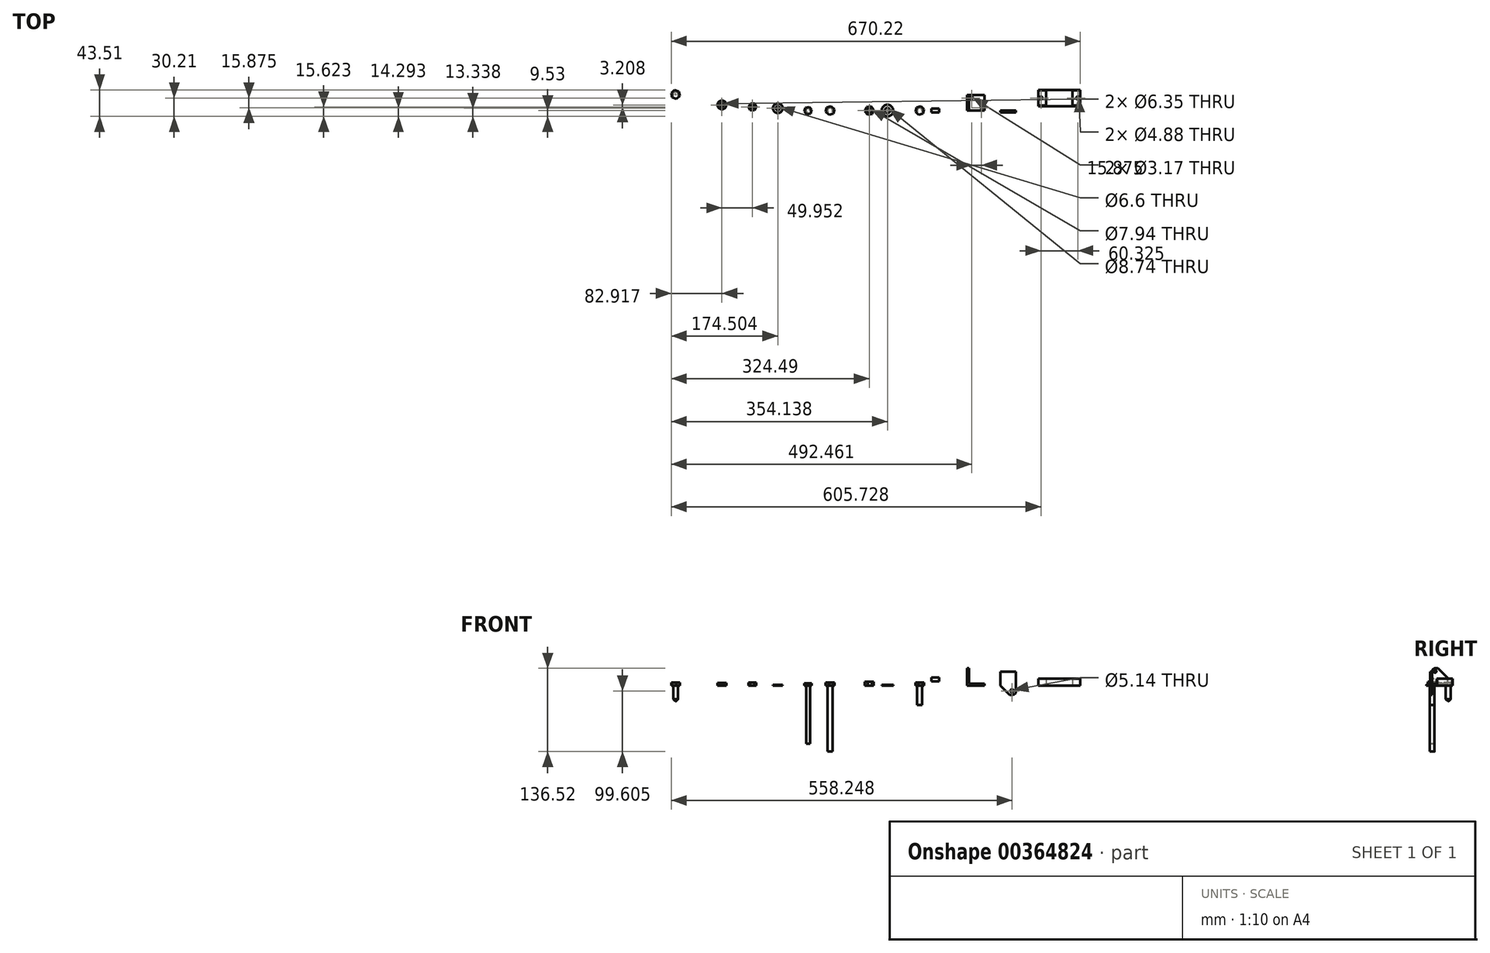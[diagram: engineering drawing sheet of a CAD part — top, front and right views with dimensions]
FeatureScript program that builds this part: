
annotation { "Feature Type Name" : "Feature", "Feature Type Description" : "" }
export const myFeature = defineFeature(function(context is Context, id is Id, definition is map)
    precondition{}
    {
        {
            var Q0;
            Q0=qCreatedBy(makeId("Right.planeOp"),FACE);
            var sketch = newSketch(context, id + "F0", { "sketchPlane" : qUnion([Q0])});
            skCircle(sketch, "E0", {"center": v(0, 10.34) * mm, "radius": 3.18 * mm});
            skSolve(sketch);
        }
        {
            var Q0;
            Q0 = qSketchRegion(id + "F0", true);
            extrude(context, id + "F1", {"entities" : qUnion([Q0]), "depth" : 12.7 * mm, "offsetDistance" : 25.4 * mm});
        }
        {
            var Q0;
            Q0=qCreatedBy(makeId("Top.planeOp"),FACE);
            var sketch = newSketch(context, id + "F2", { "sketchPlane" : qUnion([Q0])});
            skCircle(sketch, "E1", {"center": v(-19.1, 0) * mm, "radius": 3.97 * mm});
            skSolve(sketch);
        }
        {
            var Q0;
            Q0 = qSketchRegion(id + "F2", true);
            extrude(context, id + "F3", {"entities" : qUnion([Q0]), "oppositeDirection" : true, "depth" : 31.75 * mm, "offsetDistance" : 25.4 * mm});
        }
        {
            var Q0;
            Q0=makeQuery(id+"F3.opExtrude","CAP_FACE",FACE,{"disambiguationData":[OSD([sQuery(id+"F2.wireOp",EDGE,"E1")])],"isStart":true});
            var sketch = newSketch(context, id + "F4", { "sketchPlane" : qUnion([Q0])});
            skCircle(sketch, "E2.cCircle", {"center": v(-19.1, 0) * mm, "radius": 6.35 * mm, "construction": true});
            skLineSegment(sketch, "E2.0", {"start": v(-17.16, 7.07) * mm, "end": v(-12, 1.85) * mm});
            skLineSegment(sketch, "E2.1", {"start": v(-12, 1.85) * mm, "end": v(-13.95, -5.22) * mm});
            skLineSegment(sketch, "E2.2", {"start": v(-13.95, -5.22) * mm, "end": v(-21.04, -7.07) * mm});
            skLineSegment(sketch, "E2.3", {"start": v(-21.04, -7.07) * mm, "end": v(-26.2, -1.85) * mm});
            skLineSegment(sketch, "E2.4", {"start": v(-26.2, -1.85) * mm, "end": v(-24.25, 5.22) * mm});
            skLineSegment(sketch, "E2.5", {"start": v(-24.25, 5.22) * mm, "end": v(-17.16, 7.07) * mm});
            skPoint(sketch, "E2.0.midPoint", {"position": v(-14.58, 4.46) * mm});
            skSolve(sketch);
        }
        {
            var Q0;
            Q0=makeQuery(id+"F4.imprint","IMPRINT",FACE,{"disambiguationData":[TD([[makeQuery(id+"F4.imprint","IMPRINT",EDGE,{"derivedFrom":makeQuery(id+"F3.opExtrude","CAP_EDGE",EDGE,{"disambiguationData":[OSD([sQuery(id+"F2.wireOp",EDGE,"E1")])],"isStart":true})}),1.0]])]});
            var Q1;
            Q1=makeQuery(id+"F4.imprint","IMPRINT",FACE,{"disambiguationData":[TD([[makeQuery(id+"F4.imprint","IMPRINT",EDGE,{"derivedFrom":sQuery(id+"F4.wireOp",EDGE,"E2.0")}),-1.0]])]});
            extrude(context, id + "F5", {"entities" : qUnion([Q0, Q1]), "operationType" : NewBodyOperationType.ADD, "depth" : 5.16 * mm, "offsetDistance" : 25.4 * mm});
        }
        {
            var Q0;
            Q0=qCreatedBy(makeId("Top.planeOp"),FACE);
            var sketch = newSketch(context, id + "F6", { "sketchPlane" : qUnion([Q0])});
            skCircle(sketch, "E3", {"center": v(-71.95, 0) * mm, "radius": 9.53 * mm});
            skCircle(sketch, "E4", {"center": v(-71.95, 0) * mm, "radius": 4.37 * mm});
            skSolve(sketch);
        }
        {
            var Q0;
            Q0 = qSketchRegion(id + "F6", true);
            extrude(context, id + "F7", {"entities" : qUnion([Q0]), "depth" : 1.27 * mm, "offsetDistance" : 25.4 * mm});
        }
        {
            var Q0;
            Q0=qCreatedBy(makeId("Top.planeOp"),FACE);
            var sketch = newSketch(context, id + "F8", { "sketchPlane" : qUnion([Q0])});
            skCircle(sketch, "E5.cCircle", {"center": v(-101.6, 0) * mm, "radius": 6.35 * mm, "construction": true});
            skLineSegment(sketch, "E5.0", {"start": v(-98.93, 6.83) * mm, "end": v(-94.35, 1.1) * mm});
            skLineSegment(sketch, "E5.1", {"start": v(-94.35, 1.1) * mm, "end": v(-97.02, -5.73) * mm});
            skLineSegment(sketch, "E5.2", {"start": v(-97.02, -5.73) * mm, "end": v(-104.27, -6.83) * mm});
            skLineSegment(sketch, "E5.3", {"start": v(-104.27, -6.83) * mm, "end": v(-108.85, -1.1) * mm});
            skLineSegment(sketch, "E5.4", {"start": v(-108.85, -1.1) * mm, "end": v(-106.18, 5.73) * mm});
            skLineSegment(sketch, "E5.5", {"start": v(-106.18, 5.73) * mm, "end": v(-98.93, 6.83) * mm});
            skPoint(sketch, "E5.0.midPoint", {"position": v(-96.64, 3.97) * mm});
            skCircle(sketch, "E6", {"center": v(-101.6, 0) * mm, "radius": 3.97 * mm});
            skSolve(sketch);
        }
        {
            var Q0;
            Q0 = qSketchRegion(id + "F8", true);
            extrude(context, id + "F9", {"entities" : qUnion([Q0]), "depth" : 6.75 * mm, "offsetDistance" : 25.4 * mm});
        }
        {
            var Q0;
            Q0=qCreatedBy(makeId("Front.planeOp"),FACE);
            var sketch = newSketch(context, id + "F10", { "sketchPlane" : qUnion([Q0])});
            skLineSegment(sketch, "E7", {"start": v(58.43, 28.58) * mm, "end": v(58.43, 0) * mm});
            skLineSegment(sketch, "E8", {"start": v(58.43, 0) * mm, "end": v(87, 0) * mm});
            skLineSegment(sketch, "E9", {"start": v(87, 0) * mm, "end": v(87, 3.18) * mm});
            skLineSegment(sketch, "E10", {"start": v(87, 3.18) * mm, "end": v(61.6, 3.17) * mm});
            skLineSegment(sketch, "E11", {"start": v(61.6, 3.17) * mm, "end": v(61.6, 28.58) * mm});
            skLineSegment(sketch, "E12", {"start": v(61.6, 28.58) * mm, "end": v(58.43, 28.58) * mm});
            skSolve(sketch);
        }
        {
            var Q0;
            Q0 = qSketchRegion(id + "F10", true);
            extrude(context, id + "F11", {"entities" : qUnion([Q0]), "oppositeDirection" : true, "depth" : 25.4 * mm, "offsetDistance" : 25.4 * mm});
        }
        {
            var Q0;
            Q0=makeQuery(id+"F11.opExtrude","SWEPT_FACE",FACE,{"disambiguationData":[OSD([sQuery(id+"F10.wireOp",EDGE,"E10")])]});
            var sketch = newSketch(context, id + "F12", { "sketchPlane" : qUnion([Q0])});
            skLineSegment(sketch, "E13.bottom", {"start": v(66.37, 20.64) * mm, "end": v(82.25, 20.64) * mm, "construction": true});
            skLineSegment(sketch, "E13.top", {"start": v(66.37, 4.76) * mm, "end": v(82.25, 4.76) * mm, "construction": true});
            skLineSegment(sketch, "E13.left", {"start": v(66.37, 20.64) * mm, "end": v(66.37, 4.76) * mm, "construction": true});
            skLineSegment(sketch, "E13.right", {"start": v(82.25, 20.64) * mm, "end": v(82.25, 4.76) * mm, "construction": true});
            skCircle(sketch, "E14", {"center": v(66.37, 20.64) * mm, "radius": 1.59 * mm});
            skCircle(sketch, "E15", {"center": v(82.25, 4.76) * mm, "radius": 1.59 * mm});
            skSolve(sketch);
        }
        {
            var Q0;
            Q0 = qSketchRegion(id + "F12", true);
            extrude(context, id + "F13", {"entities" : qUnion([Q0]), "operationType" : NewBodyOperationType.REMOVE, "oppositeDirection" : true, "depth" : 25.4 * mm, "offsetDistance" : 25.4 * mm});
        }
        {
            var Q0;
            Q0=makeQuery(id+"F11.opExtrude","SWEPT_FACE",FACE,{"disambiguationData":[OSD([sQuery(id+"F10.wireOp",EDGE,"E7")])]});
            var sketch = newSketch(context, id + "F14", { "sketchPlane" : qUnion([Q0])});
            skCircle(sketch, "E16", {"center": v(-4.76, 23.81) * mm, "radius": 2.38 * mm});
            skSolve(sketch);
        }
        {
            var Q0;
            Q0 = qSketchRegion(id + "F14", true);
            extrude(context, id + "F15", {"entities" : qUnion([Q0]), "operationType" : NewBodyOperationType.REMOVE, "oppositeDirection" : true, "depth" : 25.4 * mm, "offsetDistance" : 25.4 * mm});
        }
        {
            var Q0;
            Q0=makeQuery(id+"F11.opExtrude","CAP_EDGE",EDGE,{"disambiguationData":[OSD([sQuery(id+"F10.wireOp",EDGE,"E12")])],"isStart":true});
            fillet(context, id + "F16", {"entities" : qUnion([Q0]), "radius" : 5.08 * mm, "tangentPropagation" : true, "allowEdgeOverflow" : false});
        }
        {
            var Q0;
            Q0=makeQuery(id+"F11.opExtrude","CAP_EDGE",EDGE,{"disambiguationData":[OSD([sQuery(id+"F10.wireOp",EDGE,"E12")])],"isStart":false});
            chamfer(context, id + "F17", {"entities" : qUnion([Q0]), "width" : 15.88 * mm, "tangentPropagation" : true});
        }
        {
            var Q0;
            Q0=qCreatedBy(makeId("Front.planeOp"),FACE);
            var sketch = newSketch(context, id + "F18", { "sketchPlane" : qUnion([Q0])});
            skLineSegment(sketch, "E17.bottom", {"start": v(113.1, 23.4) * mm, "end": v(138.5, 23.4) * mm});
            skLineSegment(sketch, "E17.top", {"start": v(113.1, -14.7) * mm, "end": v(138.5, -14.7) * mm});
            skLineSegment(sketch, "E17.left", {"start": v(113.1, 23.4) * mm, "end": v(113.1, -14.7) * mm});
            skLineSegment(sketch, "E17.right", {"start": v(138.5, 23.4) * mm, "end": v(138.5, -14.7) * mm});
            skSolve(sketch);
        }
        {
            var Q0;
            Q0 = qSketchRegion(id + "F18", true);
            extrude(context, id + "F19", {"entities" : qUnion([Q0]), "depth" : 3.17 * mm, "offsetDistance" : 25.4 * mm});
        }
        {
            var Q0;
            Q0=makeQuery(id+"F19.opExtrude","CAP_FACE",FACE,{"disambiguationData":[OSD([sQuery(id+"F18.wireOp",EDGE,"E17.bottom"),sQuery(id+"F18.wireOp",EDGE,"E17.top"),sQuery(id+"F18.wireOp",EDGE,"E17.left"),sQuery(id+"F18.wireOp",EDGE,"E17.right")])],"isStart":false});
            var sketch = newSketch(context, id + "F20", { "sketchPlane" : qUnion([Q0])});
            skCircle(sketch, "E18", {"center": v(132.16, -8.34) * mm, "radius": 2.57 * mm});
            skSolve(sketch);
        }
        {
            var Q0;
            Q0 = qSketchRegion(id + "F20", true);
            extrude(context, id + "F21", {"entities" : qUnion([Q0]), "operationType" : NewBodyOperationType.REMOVE, "oppositeDirection" : true, "depth" : 25.4 * mm, "offsetDistance" : 25.4 * mm});
        }
        {
            var Q0;
            Q0=makeQuery(id+"F19.opExtrude","SWEPT_EDGE",EDGE,{"disambiguationData":[OSD([sQuery(id+"F18.wireOp",EDGE,"E17.top"),sQuery(id+"F18.wireOp",EDGE,"E17.right")])]});
            fillet(context, id + "F22", {"entities" : qUnion([Q0]), "radius" : 5.08 * mm, "tangentPropagation" : true, "allowEdgeOverflow" : false});
        }
        {
            var Q0;
            Q0=makeQuery(id+"F19.opExtrude","SWEPT_EDGE",EDGE,{"disambiguationData":[OSD([sQuery(id+"F18.wireOp",EDGE,"E17.top"),sQuery(id+"F18.wireOp",EDGE,"E17.left")])]});
            chamfer(context, id + "F23", {"entities" : qUnion([Q0]), "width" : 15.24 * mm, "tangentPropagation" : true});
        }
        {
            var Q0;
            Q0=qCreatedBy(makeId("Top.planeOp"),FACE);
            var sketch = newSketch(context, id + "F24", { "sketchPlane" : qUnion([Q0])});
            skCircle(sketch, "E19", {"center": v(-165.9, 0) * mm, "radius": 3.97 * mm});
            skSolve(sketch);
        }
        {
            var Q0;
            Q0 = qSketchRegion(id + "F24", true);
            extrude(context, id + "F25", {"entities" : qUnion([Q0]), "oppositeDirection" : true, "depth" : 107.95 * mm, "offsetDistance" : 25.4 * mm});
        }
        {
            var Q0;
            Q0=makeQuery(id+"F25.opExtrude","CAP_FACE",FACE,{"disambiguationData":[OSD([sQuery(id+"F24.wireOp",EDGE,"E19")])],"isStart":true});
            var sketch = newSketch(context, id + "F26", { "sketchPlane" : qUnion([Q0])});
            skCircle(sketch, "E20.cCircle", {"center": v(-165.9, 0) * mm, "radius": 6.35 * mm, "construction": true});
            skLineSegment(sketch, "E20.0", {"start": v(-164.1, 7.1) * mm, "end": v(-158.84, 2) * mm});
            skLineSegment(sketch, "E20.1", {"start": v(-158.84, 2) * mm, "end": v(-160.64, -5.12) * mm});
            skLineSegment(sketch, "E20.2", {"start": v(-160.64, -5.12) * mm, "end": v(-167.7, -7.1) * mm});
            skLineSegment(sketch, "E20.3", {"start": v(-167.7, -7.1) * mm, "end": v(-172.95, -2) * mm});
            skLineSegment(sketch, "E20.4", {"start": v(-172.95, -2) * mm, "end": v(-171.15, 5.12) * mm});
            skLineSegment(sketch, "E20.5", {"start": v(-171.15, 5.12) * mm, "end": v(-164.1, 7.1) * mm});
            skPoint(sketch, "E20.0.midPoint", {"position": v(-161.46, 4.55) * mm});
            skSolve(sketch);
        }
        {
            var Q0;
            Q0 = qSketchRegion(id + "F26", true);
            extrude(context, id + "F27", {"entities" : qUnion([Q0]), "operationType" : NewBodyOperationType.ADD, "depth" : 5.16 * mm, "offsetDistance" : 25.4 * mm});
        }
        {
            var Q0;
            Q0=qCreatedBy(makeId("Top.planeOp"),FACE);
            var sketch = newSketch(context, id + "F28", { "sketchPlane" : qUnion([Q0])});
            skCircle(sketch, "E21", {"center": v(-202.1, 0) * mm, "radius": 3.18 * mm});
            skSolve(sketch);
        }
        {
            var Q0;
            Q0 = qSketchRegion(id + "F28", true);
            extrude(context, id + "F29", {"entities" : qUnion([Q0]), "oppositeDirection" : true, "depth" : 95.25 * mm, "offsetDistance" : 25.4 * mm});
        }
        {
            var Q0;
            Q0=makeQuery(id+"F29.opExtrude","CAP_FACE",FACE,{"disambiguationData":[OSD([sQuery(id+"F28.wireOp",EDGE,"E21")])],"isStart":true});
            var sketch = newSketch(context, id + "F30", { "sketchPlane" : qUnion([Q0])});
            skCircle(sketch, "E22.cCircle", {"center": v(-202.1, 0) * mm, "radius": 5.56 * mm, "construction": true});
            skLineSegment(sketch, "E22.0", {"start": v(-200.14, 6.1) * mm, "end": v(-195.83, 1.36) * mm});
            skLineSegment(sketch, "E22.1", {"start": v(-195.83, 1.36) * mm, "end": v(-197.79, -4.75) * mm});
            skLineSegment(sketch, "E22.2", {"start": v(-197.79, -4.75) * mm, "end": v(-204.06, -6.1) * mm});
            skLineSegment(sketch, "E22.3", {"start": v(-204.06, -6.1) * mm, "end": v(-208.37, -1.36) * mm});
            skLineSegment(sketch, "E22.4", {"start": v(-208.37, -1.36) * mm, "end": v(-206.4, 4.75) * mm});
            skLineSegment(sketch, "E22.5", {"start": v(-206.4, 4.75) * mm, "end": v(-200.14, 6.1) * mm});
            skPoint(sketch, "E22.0.midPoint", {"position": v(-197.98, 3.73) * mm});
            skSolve(sketch);
        }
        {
            var Q0;
            Q0=makeQuery(id+"F30.imprint","IMPRINT",FACE,{"disambiguationData":[TD([[makeQuery(id+"F30.imprint","IMPRINT",EDGE,{"derivedFrom":sQuery(id+"F30.wireOp",EDGE,"E22.0")}),-1.0]])]});
            var Q1;
            Q1=makeQuery(id+"F30.imprint","IMPRINT",FACE,{"disambiguationData":[TD([[makeQuery(id+"F30.imprint","IMPRINT",EDGE,{"derivedFrom":makeQuery(id+"F29.opExtrude","CAP_EDGE",EDGE,{"disambiguationData":[OSD([sQuery(id+"F28.wireOp",EDGE,"E21")])],"isStart":true})}),1.0]])]});
            extrude(context, id + "F31", {"entities" : qUnion([Q0, Q1]), "operationType" : NewBodyOperationType.ADD, "depth" : 3.97 * mm, "offsetDistance" : 25.4 * mm});
        }
        {
            var Q0;
            Q0=qCreatedBy(makeId("Top.planeOp"),FACE);
            var sketch = newSketch(context, id + "F32", { "sketchPlane" : qUnion([Q0])});
            skCircle(sketch, "E23", {"center": v(-251.59, 3.8) * mm, "radius": 7.94 * mm});
            skCircle(sketch, "E24", {"center": v(-251.59, 3.8) * mm, "radius": 3.3 * mm});
            skSolve(sketch);
        }
        {
            var Q0;
            Q0 = qSketchRegion(id + "F32", true);
            extrude(context, id + "F33", {"entities" : qUnion([Q0]), "depth" : 1.52 * mm, "offsetDistance" : 25.4 * mm});
        }
        {
            var Q0;
            Q0=qCreatedBy(makeId("Top.planeOp"),FACE);
            var sketch = newSketch(context, id + "F34", { "sketchPlane" : qUnion([Q0])});
            skCircle(sketch, "E25.cCircle", {"center": v(-293.22, 6.1) * mm, "radius": 5.56 * mm, "construction": true});
            skLineSegment(sketch, "E25.0", {"start": v(-289.69, 11.45) * mm, "end": v(-286.82, 5.7) * mm});
            skLineSegment(sketch, "E25.1", {"start": v(-286.82, 5.7) * mm, "end": v(-290.35, 0.35) * mm});
            skLineSegment(sketch, "E25.2", {"start": v(-290.35, 0.35) * mm, "end": v(-296.76, 0.74) * mm});
            skLineSegment(sketch, "E25.3", {"start": v(-296.76, 0.74) * mm, "end": v(-299.63, 6.48) * mm});
            skLineSegment(sketch, "E25.4", {"start": v(-299.63, 6.48) * mm, "end": v(-296.1, 11.83) * mm});
            skLineSegment(sketch, "E25.5", {"start": v(-296.1, 11.83) * mm, "end": v(-289.69, 11.45) * mm});
            skPoint(sketch, "E25.0.midPoint", {"position": v(-288.25, 8.58) * mm});
            skCircle(sketch, "E26", {"center": v(-293.22, 6.1) * mm, "radius": 3.18 * mm});
            skSolve(sketch);
        }
        {
            var Q0;
            Q0 = qSketchRegion(id + "F34", true);
            extrude(context, id + "F35", {"entities" : qUnion([Q0]), "depth" : 5.56 * mm, "offsetDistance" : 25.4 * mm});
        }
        {
            var Q0;
            Q0=qCreatedBy(makeId("Top.planeOp"),FACE);
            var sketch = newSketch(context, id + "F36", { "sketchPlane" : qUnion([Q0])});
            skCircle(sketch, "E27", {"center": v(-343.17, 9.3) * mm, "radius": 7.14 * mm});
            skCircle(sketch, "E28", {"center": v(-343.17, 9.3) * mm, "radius": 3.18 * mm});
            skSolve(sketch);
        }
        {
            var Q0;
            Q0 = qSketchRegion(id + "F36", true);
            extrude(context, id + "F37", {"entities" : qUnion([Q0]), "depth" : 4.9 * mm, "offsetDistance" : 25.4 * mm});
        }
        {
            var Q0;
            Q0=qCreatedBy(makeId("Top.planeOp"),FACE);
            var sketch = newSketch(context, id + "F38", { "sketchPlane" : qUnion([Q0])});
            skLineSegment(sketch, "E29.bottom", {"start": v(175.47, 33.98) * mm, "end": v(244.13, 33.98) * mm});
            skLineSegment(sketch, "E29.top", {"start": v(175.47, 7.39) * mm, "end": v(244.13, 7.39) * mm});
            skLineSegment(sketch, "E29.left", {"start": v(175.47, 33.98) * mm, "end": v(175.47, 7.39) * mm});
            skLineSegment(sketch, "E29.right", {"start": v(244.13, 33.98) * mm, "end": v(244.13, 7.39) * mm});
            skSolve(sketch);
        }
        {
            var Q0;
            Q0 = qSketchRegion(id + "F38", true);
            extrude(context, id + "F39", {"entities" : qUnion([Q0]), "depth" : 0.5 * mm, "offsetDistance" : 25.4 * mm});
        }
        {
            var Q0;
            Q0=makeQuery(id+"F39.opExtrude","CAP_FACE",FACE,{"disambiguationData":[OSD([sQuery(id+"F38.wireOp",EDGE,"E29.bottom"),sQuery(id+"F38.wireOp",EDGE,"E29.top"),sQuery(id+"F38.wireOp",EDGE,"E29.left"),sQuery(id+"F38.wireOp",EDGE,"E29.right")])],"isStart":false});
            var sketch = newSketch(context, id + "F40", { "sketchPlane" : qUnion([Q0])});
            skLineSegment(sketch, "E30.bottom", {"start": v(175.47, 33.98) * mm, "end": v(244.13, 33.98) * mm});
            skLineSegment(sketch, "E30.top", {"start": v(175.47, 32.88) * mm, "end": v(244.13, 32.88) * mm});
            skLineSegment(sketch, "E30.left", {"start": v(175.47, 33.98) * mm, "end": v(175.47, 32.88) * mm});
            skLineSegment(sketch, "E30.right", {"start": v(244.13, 33.98) * mm, "end": v(244.13, 32.88) * mm});
            skLineSegment(sketch, "E31.bottom", {"start": v(244.13, 7.39) * mm, "end": v(175.47, 7.39) * mm});
            skLineSegment(sketch, "E31.top", {"start": v(244.13, 8.22) * mm, "end": v(175.47, 8.22) * mm});
            skLineSegment(sketch, "E31.left", {"start": v(244.13, 7.39) * mm, "end": v(244.13, 8.22) * mm});
            skLineSegment(sketch, "E31.right", {"start": v(175.47, 7.39) * mm, "end": v(175.47, 8.22) * mm});
            skLineSegment(sketch, "E32.bottom", {"start": v(188.16, 32.88) * mm, "end": v(231.57, 32.88) * mm});
            skLineSegment(sketch, "E32.top", {"start": v(188.16, 8.22) * mm, "end": v(231.57, 8.22) * mm});
            skLineSegment(sketch, "E32.left", {"start": v(188.16, 32.88) * mm, "end": v(188.16, 8.22) * mm});
            skLineSegment(sketch, "E32.right", {"start": v(231.57, 32.88) * mm, "end": v(231.57, 8.22) * mm});
            skSolve(sketch);
        }
        {
            var Q0;
            Q0 = qSketchRegion(id + "F40", true);
            extrude(context, id + "F41", {"entities" : qUnion([Q0]), "operationType" : NewBodyOperationType.ADD, "depth" : 11.1 * mm, "offsetDistance" : 25.4 * mm});
        }
        {
            var Q0;
            Q0=makeQuery(id+"F39.opExtrude","CAP_FACE",FACE,{"disambiguationData":[OSD([sQuery(id+"F38.wireOp",EDGE,"E29.bottom"),sQuery(id+"F38.wireOp",EDGE,"E29.top"),sQuery(id+"F38.wireOp",EDGE,"E29.left"),sQuery(id+"F38.wireOp",EDGE,"E29.right")])],"isStart":true});
            var sketch = newSketch(context, id + "F42", { "sketchPlane" : qUnion([Q0])});
            skLineSegment(sketch, "E33", {"start": v(247.51, -20.68) * mm, "end": v(172.82, -20.68) * mm, "construction": true});
            skPoint(sketch, "E33.startSnap0", {"position": v(244.13, -20.68) * mm});
            skCircle(sketch, "E34", {"center": v(239.96, -20.68) * mm, "radius": 2.44 * mm});
            skCircle(sketch, "E35", {"center": v(179.64, -20.68) * mm, "radius": 2.44 * mm});
            skSolve(sketch);
        }
        {
            var Q0;
            Q0 = qSketchRegion(id + "F42", true);
            extrude(context, id + "F43", {"entities" : qUnion([Q0]), "operationType" : NewBodyOperationType.REMOVE, "oppositeDirection" : true, "depth" : 25.4 * mm, "offsetDistance" : 25.4 * mm});
        }
        {
            var Q0;
            Q0=qCreatedBy(makeId("Top.planeOp"),FACE);
            var sketch = newSketch(context, id + "F44", { "sketchPlane" : qUnion([Q0])});
            skCircle(sketch, "E36", {"center": v(-419.12, 26.47) * mm, "radius": 3.97 * mm});
            skSolve(sketch);
        }
        {
            var Q0;
            Q0 = qSketchRegion(id + "F44", true);
            extrude(context, id + "F45", {"entities" : qUnion([Q0]), "oppositeDirection" : true, "depth" : 25.4 * mm, "offsetDistance" : 25.4 * mm});
        }
        {
            var Q0;
            Q0=makeQuery(id+"F45.opExtrude","CAP_FACE",FACE,{"disambiguationData":[OSD([sQuery(id+"F44.wireOp",EDGE,"E36")])],"isStart":true});
            var sketch = newSketch(context, id + "F46", { "sketchPlane" : qUnion([Q0])});
            skCircle(sketch, "E37.cCircle", {"center": v(-419.12, 26.47) * mm, "radius": 6.35 * mm, "construction": true});
            skLineSegment(sketch, "E37.0", {"start": v(-412.16, 24.18) * mm, "end": v(-417.62, 19.3) * mm});
            skLineSegment(sketch, "E37.1", {"start": v(-417.62, 19.3) * mm, "end": v(-424.59, 21.59) * mm});
            skLineSegment(sketch, "E37.2", {"start": v(-424.59, 21.59) * mm, "end": v(-426.09, 28.76) * mm});
            skLineSegment(sketch, "E37.3", {"start": v(-426.09, 28.76) * mm, "end": v(-420.62, 33.65) * mm});
            skLineSegment(sketch, "E37.4", {"start": v(-420.62, 33.65) * mm, "end": v(-413.66, 31.36) * mm});
            skLineSegment(sketch, "E37.5", {"start": v(-413.66, 31.36) * mm, "end": v(-412.16, 24.18) * mm});
            skPoint(sketch, "E37.0.midPoint", {"position": v(-414.89, 21.74) * mm});
            skSolve(sketch);
        }
        {
            var Q0;
            Q0 = qSketchRegion(id + "F46", true);
            extrude(context, id + "F47", {"entities" : qUnion([Q0]), "operationType" : NewBodyOperationType.ADD, "depth" : 5.56 * mm, "offsetDistance" : 25.4 * mm});
        }
        {
            var Q0;
            Q0=makeQuery(id+"F45.opExtrude","CAP_EDGE",EDGE,{"disambiguationData":[OSD([sQuery(id+"F44.wireOp",EDGE,"E36")])],"isStart":false});
            chamfer(context, id + "F48", {"entities" : qUnion([Q0]), "width" : 3.3 * mm, "tangentPropagation" : true});
        }
    });
